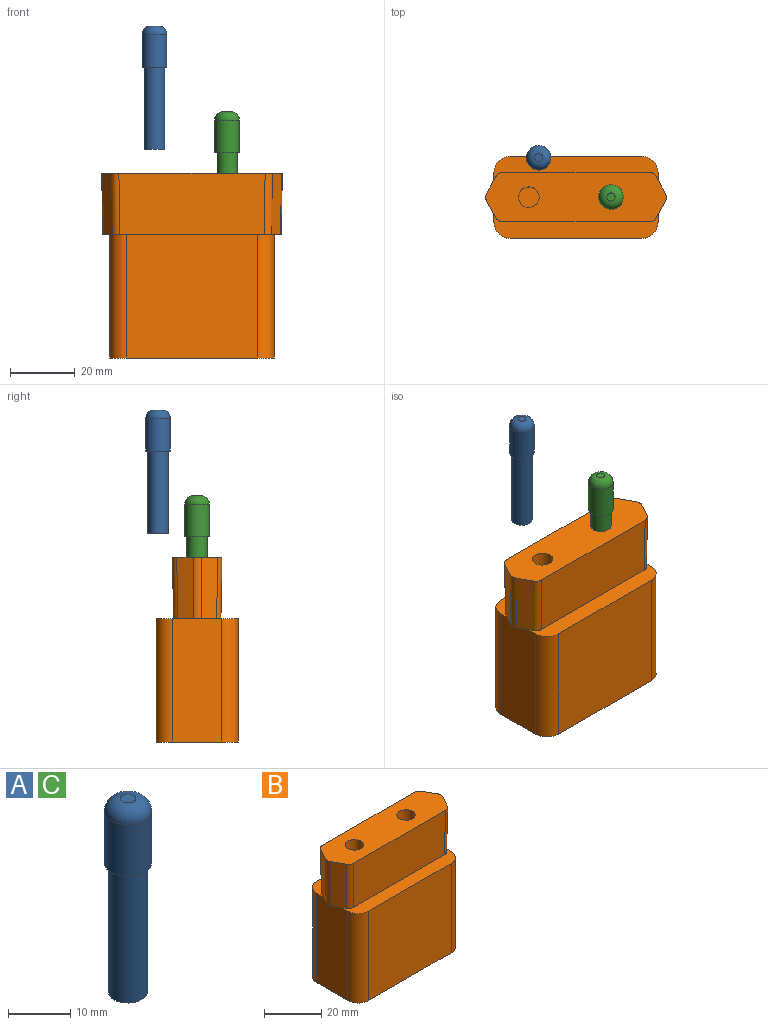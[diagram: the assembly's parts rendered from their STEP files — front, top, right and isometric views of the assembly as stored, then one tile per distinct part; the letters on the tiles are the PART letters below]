
ASSEMBLY  parts=3 mates=1
PART A: 6 faces, bbox 7.6x7.6x38.1 mm
  f0: cylinder r=3.17mm len=25.4mm, axis (0,0,-1), area 506.7mm2, adj f1,f3
  f1: plane 6.35x6.35mm, normal (0,0,-1), area 31.7mm2, adj f0
  f2: cylinder r=3.81mm len=10.16mm, axis (0,0,1), area 243.2mm2, adj f3,f5
  f3: plane 7.62x7.62mm, normal (0,0,-1), area 13.9mm2, adj f0,f2
  f4: plane 2.54x2.54mm, normal (0,0,1), area 5.1mm2, adj f5
  f5: torus R=1.27mm, axis (0,0,1), area 72.4mm2, adj f2,f4
PART B: 40 faces, bbox 55.9x25.4x57.2 mm
  f0: plane 50.8x25.4mm, normal (0,0,-1), area 1113.3mm2, adj f3,f4,f5,f6,f7,f8,f9,f10
  f1: plane 50.81x8.07mm, normal (0,0,1), area 266.2mm2, adj f3,f4,f6,f7,f10,f15,f16,f17
  f2: plane 50.81x8.07mm, normal (0,0,1), area 266.2mm2, adj f4,f5,f6,f8,f9,f12,f13,f14
  f3: plane 40.64x38.1mm, normal (0,-1,0), area 1548.4mm2, adj f0,f1,f7,f10
  f4: plane 38.1x15.24mm, normal (1,0,0), area 580.6mm2, adj f0,f1,f2,f7,f8,f11
  f5: plane 40.64x38.1mm, normal (0,1,0), area 1548.4mm2, adj f0,f2,f8,f9
  f6: plane 38.1x15.24mm, normal (-1,0,0), area 580.6mm2, adj f0,f1,f2,f9,f10,f19
  f7: cylinder r=5.08mm len=38.1mm, axis (0,0,1), area 304mm2, adj f0,f1,f3,f4
  f8: cylinder r=5.08mm len=38.1mm, axis (0,0,-1), area 304mm2, adj f0,f2,f4,f5
  f9: cylinder r=5.08mm len=38.1mm, axis (0,0,1), area 304mm2, adj f0,f2,f5,f6
  f10: cylinder r=5.08mm len=38.1mm, axis (0,0,-1), area 304mm2, adj f0,f1,f3,f6
  f11: plane 9.29x2.2mm, normal (0,0,-1), area 11.5mm2, adj f4,f12,f17,f20
  f12: plane 19.05x5.13mm, normal (0.88,0.48,-0.02), area 107.8mm2, adj f2,f11,f18,f20,f22
  f13: plane 45.23x19.05mm, normal (0,1,-0.02), area 858.1mm2, adj f2,f18,f22,f23
  f14: plane 19.05x5.13mm, normal (-0.88,0.48,-0.02), area 107.8mm2, adj f2,f18,f19,f21,f23
  f15: plane 19.05x5.13mm, normal (-0.88,-0.48,-0.02), area 107.8mm2, adj f1,f18,f19,f21,f24
  f16: plane 45.23x19.05mm, normal (0,-1,-0.02), area 858.1mm2, adj f1,f18,f24,f25
  f17: plane 19.05x5.13mm, normal (0.88,-0.48,-0.02), area 107.8mm2, adj f1,f11,f18,f20,f25
  f18: plane 55.94x15.35mm, normal (0,0,1), area 738.7mm2, adj f12,f13,f14,f15,f16,f17,f20,f21
  f19: plane 9.29x2.2mm, normal (0,0,-1), area 11.5mm2, adj f6,f14,f15,f21
  f20: cylinder r=2.54mm len=19.06mm, axis (-0.02,0,-1), area 48.5mm2, adj f11,f12,f17,f18
  f21: cylinder r=2.54mm len=19.06mm, axis (0.02,0,-1), area 48.5mm2, adj f14,f15,f18,f19
  f22: cylinder r=2.54mm len=19.06mm, axis (-0.01,-0.02,-1), area 51.8mm2, adj f2,f12,f13,f18
  f23: cylinder r=2.54mm len=19.06mm, axis (0.01,-0.02,-1), area 51.8mm2, adj f2,f13,f14,f18
  f24: cylinder r=2.54mm len=19.06mm, axis (0.01,0.02,-1), area 51.8mm2, adj f1,f15,f16,f18
  f25: cylinder r=2.54mm len=19.06mm, axis (-0.01,0.02,-1), area 51.8mm2, adj f1,f16,f17,f18
  f26: plane 6.35x6.35mm, normal (0,0,1), area 31.7mm2, adj f27
  f27: cylinder r=3.17mm len=19.05mm, axis (0,0,1), area 380mm2, adj f18,f26
  f28: plane 6.35x6.35mm, normal (0,0,1), area 31.7mm2, adj f29
  f29: cylinder r=3.17mm len=19.05mm, axis (0,0,1), area 380mm2, adj f18,f28
  f30: plane 15.24x12.7mm, normal (0,-1,0), area 193.5mm2, adj f0,f31,f33,f34
  f31: plane 12.7x5.08mm, normal (-1,0,0), area 64.5mm2, adj f0,f30,f32,f34
  f32: plane 15.24x12.7mm, normal (0,1,0), area 193.5mm2, adj f0,f31,f33,f34
  f33: plane 12.7x5.08mm, normal (1,0,0), area 64.5mm2, adj f0,f30,f32,f34
  f34: plane 15.24x5.08mm, normal (0,0,-1), area 77.4mm2, adj f30,f31,f32,f33
  f35: plane 15.24x12.7mm, normal (0,1,0), area 193.5mm2, adj f0,f36,f38,f39
  f36: plane 12.7x5.08mm, normal (1,0,0), area 64.5mm2, adj f0,f35,f37,f39
  f37: plane 15.24x12.7mm, normal (0,-1,0), area 193.5mm2, adj f0,f36,f38,f39
  f38: plane 12.7x5.08mm, normal (-1,0,0), area 64.5mm2, adj f0,f35,f37,f39
  f39: plane 15.24x5.08mm, normal (0,0,-1), area 77.4mm2, adj f35,f36,f37,f38
PART C: same geometry as A
PLACE A t=(-31.86,15.2,58.04)mm
PLACE B t=(-22.15,2.92,-6.62)mm fixed
PLACE C t=(-9.45,3.08,31.48)mm
MATE cylindrical C.f0 <-> B.f27  axis (0,0,-1) through (-9.45,2.92,31.48)mm
